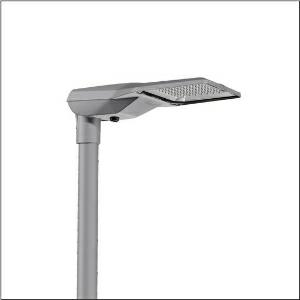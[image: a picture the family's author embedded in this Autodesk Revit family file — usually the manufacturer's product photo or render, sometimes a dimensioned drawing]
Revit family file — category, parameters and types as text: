
# Revit family: streetlight_sl_21_midi___p0_5a_5xe3v33r08lb_9200
name_source: partatom
category: Lighting Fixtures
units: mm (PartAtom-declared; Revit-internal decimal feet)

## family parameters
Cut with Voids When Loaded = No
Host = Face
Light Source = No
Part Type = Normal
Room Calculation Point = No
Round Connector Dimension = Use Diameter
Shared = No

## types (1)
- --- (1 x LED, 14100 lm, 99.6 W, 3000K)
    Apparent Load = 100 VA
    CIE Flux Codes = 37 73 96 100 100
    Color Rendering = 70
    Color Temperature = 3000K
    Default Elevation = 1800 mm
    Description = Streetlight SL 21 midi, mast luminaire, primary light control with lens, of PMMA, primary optical cover: cover, of toughened safety glass, transparent, light distribution: P0.5a, light emission: direct distribution, primary light characteristic: asymmetric, installation type: post-top, side-entry, LED, High Power LED, rated luminous flux: 14.100lm, luminous efficacy: 142lm/W, light colour: 730, colour temperature: 3000K, control gear: D4i, control: pre-setting: logarithmic dimming characteristic, flexible luminous flux parameterisation, time-dependent luminous flux control, constant luminous flux control, overheat protection, mains connection: 230..240V, AC, 50/60Hz, start of lifetime: 100W, end of service life: 102W, reduction: 46W, luminaire housing, of diecast aluminium, powder-coated, Siteco® metallic grey (DB 702S), corrosivity category C5 mid according to DIN EN ISO 12944, multi-level sealing system, sealing non-destructively replaceable, inclination adjustable: 0°, 5°, 10°, 15°, please order mast flange separately, length: 644mm, width: 335mm, height: 110mm, mast flange for spigot size: 42mm (side-entry): 5XC10008XM4, 60/48mm (side-entry/post-top): 5XC10108XM2, 76/60mm (side-entry/post-top): 5XC10108XM1, mounting height: 4..8m, Smart Interface below, protection rating (complete): IP66, insulation class (complete): insulation class II (safety insulation), certification: CE, ENEC, ENEC+, VDE, impact resistance: IK10, permissible operating ambient temperature for outdoor applications: -40..+50°C, standard-compliant lighting for roads and squares, packaging unit: 1 piece

Light Distribution: P0.5a
    Height = 111 mm
    Lamp = 1 x LED
    Lamp Light Flux = 14100 lm
    Lamp Power = 99.6 W
    Lamp count = 1
    Length = 644 mm
    Luminous efficacy = 142 lm/W
    Manufacturer = Siteco
    ModVariant = No
    Model = 5XE3V33R08LB
    Number of Poles = 1
    OnlyDefault = Yes
    Power Factor = 1
    Product Name = Streetlight SL 21 midi | P0.5a
    Product group = mast luminaire | pylon top
    ProductGroupID = 6100
    Protection Class = Protection class II
    Protection Degree = IP 66
    RLX_Detail_Level = 1
    RLX_Emergency_Light_Flux = 0 lm
    RLX_Emergency_Type = 0
    RLX_Emergency_Type_DB = No
    RlxData = <blob elided: 26425 chars, md5=ec264fe9>
    Socket = socket
    Standby Power = 0 W
    System Light Flux = 14100 lm
    System Power = 100 W
    Type Comments = factory setting: luminous flux: 100 % | dim-lin: 254 | 1020 mA
    Type Image = l_1004300.jpg
    URL = http://relux.com
    VarID = @adj_013129
    Voltage = 0 V
    Weight = 0.00 kg
    Width = 336 mm

## geometry (parser evidence)
native form markers: Blend x4, Sweep x9
no freeform markers — native parametric forms only
